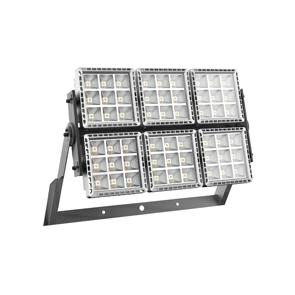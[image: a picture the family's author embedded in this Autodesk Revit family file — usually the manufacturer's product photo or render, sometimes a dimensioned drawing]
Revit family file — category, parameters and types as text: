
# Revit family: Lighting-Floodlights-GEWISS-SMART[PRO]2.0-LED-HIGH-POWER_6MODULE_CLI
name_source: partatom
category: Apparecchi per illuminazione
units: mm (PartAtom-declared; Revit-internal decimal feet)

## family parameters
Condiviso = No
Host = Superficie
Punto di calcolo locali = No
Quota connettore circolare = Usa diametro
Sorgente d'illuminazione = No
Taglio con vuoti quando caricato = No
Tipo di parte = Normale

## types (54) — shared parameters
Application = Indoor / Outdoor
Body = Die-cast aluminium -
Carico apparente = 1020 VA
Catalogue = LIGHTING
Classification: = -
Classificazione = Lighting
Colour = Graphite grey
Colour : = Polyester powder coated
Commenti Wattaggio 1_100 = Sì
Commenti Wattaggio 1_200 = No
Commenti sul wattaggio = 1020W
Context = Sport, Big Areas
Control System = See external supply unit
DIN 18032-3 certification = -
Device with reduced surface temperature = No
Driver = To be ordered separately
Driver Box = External
Eletrical and lighting features = -
Etichetta wattaggio = Sì
External screw = Stainless steel
Fine staffa = 484 mm  [stored 1.58793 ft]
Fixing = Bracket
Gasket = Anti-aging silicone
General information = -
Glow Wire Test : = -
H_centro_STaffa = 459 mm  [stored 1.50591 ft]
IDF = 6be5a8cc-6c55-4606-870e-3d78fd827b65
IDT = 5694ef43a41d4293b3b9519a64b0ddb9
IP degree = IP66
Immagine tipo = SMART PRO 6.jpg
Installationa and maintenance = -
Insulation class = I
LED Maintenance = Yes
L_plafoniera = 817 mm
Lampada = LED
Larghezza = 503 mm  [stored 1.65026 ft]
Lifetime = L90B10 (Tq+25°C) = 36000h L90B10 (Tq+50°C) = 26000h L80B10 (Tq+25°C) = 81000h
Locking Hook = Hexagonal metric screws
Luminaire = LED luminaire with mid and high lumen power
Materials = -
Maximum surface exposed to the wind : = 0,333 m2
Mouting and installation = High-mast lighting - Wall mounting - Ground mouting
N. poli = 2
Operating temperature : = -30 +50 °C
Optic Maintenance = Not available
Optic and illuminating features = -
Ottica_ = GEWISS - OTTICA
Overvoltage protection = See external supply unit
Photobiological Risk Class = -
Produttore = GEWISS S.p.A.
Prospetto di default = 1219 mm
Rated frequency (Hz) = -
SEO = Floodlight
Shield type = Flat tempered glass 4mm
Shock resistance = IK08
Spessore staffa = 59 mm  [stored 0.19357 ft]
Standard- = EN60598-1; EN60598-2-5; IEC 62778; IEC 62471; EN13201
Standards and approvals = -
Stocking temperature = -
Struttura = GEWISS - NERO
Struttura plafoniera = GEWISS - PLAFONIERA
Supply voltage = -
System power = 970W
Technical sheet = https://www.gewiss.com
Tilt- = Rotation on bracket with integrated goniometer
Trasformatore = GEWISS - PLAFONIERA
Type of light source = LED - Not replaceable
URL = https://www.gewiss.com
Unique digital code (Datamatrix) = Currently not present
Version file RFA = 20.11
Vetro acceso = Lampada accesa
Voltaggio = 230 V
Warranty = 5 years
Weight (kg): = 29
Wiring = Watertight connector

## per-type parameters (varying)
| type | Color Rendering Index | Colour temperature | Descrizione | Efficiency (lm/W) | IPEA | Lumen output (lm) | Modello | Optic | Optic : | Standard Deviation Colour Matching | Unified Glare Rating | Versions |
| GWP2630AF757 - SMART PRO 3x2M A2 CRI70 5700K | CRI-70 | 5700K | SMART PRO 3x2M A2 CRI70 5700K | 101 | ROAD = B // LARGE AREAS = A + // CYCLOPEDONALS = A // GREEN AREAS = A // HISTORICAL CENTER = A ++ // OTHER = A ++ | 98200 | GWP2630AF757 | A2 - Asymmetrical Medium | Polished anodised aluminum reflector with 99.99% pure aluminum | SDCM = 5 | G*3 - ULOR = 0 | 5700K cold light |
| GWP2630AH740 - SMART PRO 3x2M C3 CRI70 4000K | CRI-70 | 4000K | SMART PRO 3x2M C3 CRI70 4000K | 126 | ROAD = A + // LARGE AREAS = A4 + // CYCLOPEDONALS = A ++ // GREEN AREAS = A ++ // HISTORICAL CENTER = A5 + // OTHER = A5 + | 122700 | GWP2630AH740 | C3 - Circular 20° | Polished quartz and metallized PC HT reflector | SDCM = 5 | G*6 - ULOR = 0 | 4000K natural light |
| GWP2630AB857 - SMART PRO 3x2M S2 CRI80 5700K | CRI-80 | 5700K | SMART PRO 3x2M S2 CRI80 5700K | 117 | ROAD = A // LARGE AREAS = A3 + // CYCLOPEDONALS = A + // GREEN AREAS = A + // HISTORICAL CENTER = A4 + // OTHER = A4 + | 113700 | GWP2630AB857 | S2 - Symmetric Medium | Polished anodised aluminum reflector with 99.99% pure aluminum | SDCM = 3 | G*6 - ULOR = 0 | 5700K cold light |
| GWP2630AB740 - SMART PRO 3x2M S2 CRI70 4000K | CRI-70 | 4000K | SMART PRO 3x2M S2 CRI70 4000K | 126 | ROAD = A + // LARGE AREAS = A4 + // CYCLOPEDONALS = A ++ // GREEN AREAS = A ++ // HISTORICAL CENTER = A5 + // OTHER = A5 + | 121800 | GWP2630AB740 | S2 - Symmetric Medium | Polished anodised aluminum reflector with 99.99% pure aluminum | SDCM = 5 | G*6 - ULOR = 0 | 4000K natural light |
| GWP2630AC957 - SMART PRO 3x2M A1 CRI90 5700K | CRI-90 TLCI-80 | 5700K | SMART PRO 3x2M A1 CRI90 5700K | 94 | ROAD = C // LARGE AREAS = A // CYCLOPEDONALS = B // GREEN AREAS = B // HISTORICAL CENTER = A + // OTHER = A + | 91400 | GWP2630AC957 | A1 - Asymmetrical Wide | Polished quartz and metallized PC HT reflector | SDCM = 3 | G*4 - ULOR = 0 | 5700K cold light |
| GWP2630AB840 - SMART PRO 3x2M S2 CRI80 4000K | CRI-80 | 4000K | SMART PRO 3x2M S2 CRI80 4000K | 117 | ROAD = A // LARGE AREAS = A3 + // CYCLOPEDONALS = A + // GREEN AREAS = A + // HISTORICAL CENTER = A4 + // OTHER = A4 + | 113700 | GWP2630AB840 | S2 - Symmetric Medium | Polished anodised aluminum reflector with 99.99% pure aluminum | SDCM = 3 | G*6 - ULOR = 0 | 4000K natural light |
| GWP2630AH957 - SMART PRO 3x2M C3 CRI90 5700K | CRI-90 TLCI-80 | 5700K | SMART PRO 3x2M C3 CRI90 5700K | 101 | ROAD = B // LARGE AREAS = A + // CYCLOPEDONALS = A // GREEN AREAS = A // HISTORICAL CENTER = A ++ // OTHER = A ++ | 98200 | GWP2630AH957 | C3 - Circular 20° | Polished quartz and metallized PC HT reflector | SDCM = 3 | G*6 - ULOR = 0 | 5700K cold light |
| GWP2630AL857 - SMART PRO 3x2M C2 CRI80 5700K | CRI-80 | 5700K | SMART PRO 3x2M C2 CRI80 5700K | 115 | ROAD = A // LARGE AREAS = A ++ // CYCLOPEDONALS = A + // GREEN AREAS = A + // HISTORICAL CENTER = A4 + // OTHER = A4 + | 111900 | GWP2630AL857 | C2 - Circular 25° | Polished quartz and metallized PC HT reflector | SDCM = 3 | G*6 - ULOR = 0 | 5700K cold light |
| GWP2630AF857 - SMART PRO 3x2M A2 CRI80 5700K | CRI-80 | 5700K | SMART PRO 3x2M A2 CRI80 5700K | 95 | ROAD = C // LARGE AREAS = A // CYCLOPEDONALS = B // GREEN AREAS = B // HISTORICAL CENTER = A + // OTHER = A + | 91700 | GWP2630AF857 | A2 - Asymmetrical Medium | Polished anodised aluminum reflector with 99.99% pure aluminum | SDCM = 3 | G*3 - ULOR = 0 | 5700K cold light |
| GWP2630AN740 - SMART PRO 3x2M A3 CRI70 4000K | CRI-70 | 4000K | SMART PRO 3x2M A3 CRI70 4000K | 123 | ROAD = A + // LARGE AREAS = A3 + // CYCLOPEDONALS = A ++ // GREEN AREAS = A ++ // HISTORICAL CENTER = A5 + // OTHER = A5 + | 119400 | GWP2630AN740 | A3 - Assymetric Narrow | Polished anodised aluminum reflector with 99.99% pure aluminum | SDCM = 5 | G*6 - ULOR = 0 | 4000K natural light |
| GWP2630AG757 - SMART PRO 3x2M C4 CRI70 5700K | CRI-70 | 5700K | SMART PRO 3x2M C4 CRI70 5700K | 126 | ROAD = A + // LARGE AREAS = A4 + // CYCLOPEDONALS = A ++ // GREEN AREAS = A ++ // HISTORICAL CENTER = A5 + // OTHER = A5 + | 122700 | GWP2630AG757 | C4 - Circular 15° | Polished quartz and metallized PC HT reflector | SDCM = 5 | G*6 - ULOR = 0 | 5700K cold light |
| GWP2630AG840 - SMART PRO 3x2M C4 CRI80 4000K | CRI-80 | 4000K | SMART PRO 3x2M C4 CRI80 4000K | 118 | ROAD = A // LARGE AREAS = A3 + // CYCLOPEDONALS = A + // GREEN AREAS = A + // HISTORICAL CENTER = A4 + // OTHER = A4 + | 114500 | GWP2630AG840 | C4 - Circular 15° | Polished quartz and metallized PC HT reflector | SDCM = 3 | G*6 - ULOR = 0 | 4000K natural light |
| GWP2630AF840 - SMART PRO 3x2M A2 CRI80 4000K | CRI-80 | 4000K | SMART PRO 3x2M A2 CRI80 4000K | 95 | ROAD = C // LARGE AREAS = A // CYCLOPEDONALS = B // GREEN AREAS = B // HISTORICAL CENTER = A + // OTHER = A + | 91700 | GWP2630AF840 | A2 - Asymmetrical Medium | Polished anodised aluminum reflector with 99.99% pure aluminum | SDCM = 3 | G*3 - ULOR = 0 | 4000K natural light |
| GWP2630AM957 - SMART PRO 3x2M C1 CRI90 5700K | CRI-90 TLCI-80 | 5700K | SMART PRO 3x2M C1 CRI90 5700K | 99 | ROAD = C // LARGE AREAS = A // CICLOPEDONALI = B // GREEN AREAS = B // HISTORICAL CENTER = A ++ // OTHER = A ++ | 95900 | GWP2630AM957 | C1 - Circular 30° | Polished quartz and metallized PC HT reflector | SDCM = 3 | G*6 - ULOR = 0 | 5700K cold light |
| GWP2630AN757 - SMART PRO 3x2M A3 CRI70 5700K | CRI-70 | 5700K | SMART PRO 3x2M A3 CRI70 5700K | 123 | ROAD = A + // LARGE AREAS = A3 + // CYCLOPEDONALS = A ++ // GREEN AREAS = A ++ // HISTORICAL CENTER = A5 + // OTHER = A5 + | 119400 | GWP2630AN757 | A3 - Assymetric Narrow | Polished anodised aluminum reflector with 99.99% pure aluminum | SDCM = 5 | G*6 - ULOR = 0 | 5700K cold light |
| GWP2630AM740 - SMART PRO 3x2M C1 CRI70 4000K | CRI-70 | 4000K | SMART PRO 3x2M C1 CRI70 4000K | 124 | ROAD = A + // LARGE AREAS = A3 + // CYCLOPEDONALS = A ++ // GREEN AREAS = A ++ // HISTORICAL CENTER = A5 + // OTHER = A5 + | 119900 | GWP2630AM740 | C1 - Circular 30° | Polished quartz and metallized PC HT reflector | SDCM = 5 | G*6 - ULOR = 0 | 4000K natural light |
| GWP2630AF730 - SMART PRO 3x2M A2 CRI70 3000K | CRI-70 | 3000K | SMART PRO 3x2M A2 CRI70 3000K | 95 | ROAD = C // LARGE AREAS = A // CYCLOPEDONALS = B // GREEN AREAS = B // HISTORICAL CENTER = A + // OTHER = A + | 91700 | GWP2630AF730 | A2 - Asymmetrical Medium | Polished anodised aluminum reflector with 99.99% pure aluminum | SDCM = 5 | G*3 - ULOR = 0 | 3000K warm light |
| GWP2630AL757 - SMART PRO 3x2M C2 CRI70 5700K | CRI-70 | 5700K | SMART PRO 3x2M C2 CRI70 5700K | 124 | ROAD = A + // LARGE AREAS = A3 + // CYCLOPEDONALS = A ++ // GREEN AREAS = A ++ // HISTORICAL CENTER = A5 + // OTHER = A5 + | 119900 | GWP2630AL757 | C2 - Circular 25° | Polished quartz and metallized PC HT reflector | SDCM = 5 | G*6 - ULOR = 0 | 5700K cold light |
| GWP2630AN857 - SMART PRO 3x2M A3 CRI80 5700K | CRI-80 | 5700K | SMART PRO 3x2M A3 CRI80 5700K | 115 | ROAD = A // LARGE AREAS = A ++ // CYCLOPEDONALS = A + // GREEN AREAS = A + // HISTORICAL CENTER = A4 + // OTHER = A4 + | 111400 | GWP2630AN857 | A3 - Assymetric Narrow | Polished anodised aluminum reflector with 99.99% pure aluminum | SDCM = 3 | G*6 - ULOR = 0 | 5700K cold light |
| GWP2630AB957 - SMART PRO 3x2M S2 CRI90 5700K | CRI-90 TLCI-80 | 5700K | SMART PRO 3x2M S2 CRI90 5700K | 100 | ROAD = B // LARGE AREAS = A + // CYCLOPEDONALS = B // GREEN AREAS = B // HISTORICAL CENTER = A ++ // OTHER = A ++ | 97400 | GWP2630AB957 | S2 - Symmetric Medium | Polished anodised aluminum reflector with 99.99% pure aluminum | SDCM = 3 | G*6 - ULOR = 0 | 5700K cold light |
| GWP2630AL730 - SMART PRO 3x2M C2 CRI70 3000K | CRI-70 | 3000K | SMART PRO 3x2M C2 CRI70 3000K | 115 | ROAD = A // LARGE AREAS = A ++ // CYCLOPEDONALS = A + // GREEN AREAS = A + // HISTORICAL CENTER = A4 + // OTHER = A4 + | 111900 | GWP2630AL730 | C2 - Circular 25° | Polished quartz and metallized PC HT reflector | SDCM = 5 | G*6 - ULOR = 0 | 3000K warm light |
| GWP2630AC857 - SMART PRO 3x2M A1 CRI80 5700K | CRI-80 | 5700K | SMART PRO 3x2M A1 CRI80 5700K | 110 | ROAD = A // LARGE AREAS = A ++ // CYCLOPEDONALS = A // GREEN AREAS = A // HISTORICAL CENTER = A3 + // OTHER = A3 + | 106600 | GWP2630AC857 | A1 - Asymmetrical Wide | Polished quartz and metallized PC HT reflector | SDCM = 3 | G*4 - ULOR = 0 | 5700K cold light |
| GWP2630AB730 - SMART PRO 3x2M S2 CRI70 3000K | CRI-70 | 3000K | SMART PRO 3x2M S2 CRI70 3000K | 117 | ROAD = A // LARGE AREAS = A3 + // CYCLOPEDONALS = A + // GREEN AREAS = A + // HISTORICAL CENTER = A4 + // OTHER = A4 + | 113700 | GWP2630AB730 | S2 - Symmetric Medium | Polished anodised aluminum reflector with 99.99% pure aluminum | SDCM = 5 | G*6 - ULOR = 0 | 3000K warm light |
| GWP2630AC730 - SMART PRO 3x2M A1 CRI70 3000K | CRI-70 | 3000K | SMART PRO 3x2M A1 CRI70 3000K | 110 | ROAD = A // LARGE AREAS = A ++ // CYCLOPEDONALS = A // GREEN AREAS = A // HISTORICAL CENTER = A3 + // OTHER = A3 + | 106600 | GWP2630AC730 | A1 - Asymmetrical Wide | Polished quartz and metallized PC HT reflector | SDCM = 5 | G*4 - ULOR = 0 | 3000K warm light |
| GWP2630AA957 - SMART PRO 3x2M S1 CRI90 5700K | CRI-90 TLCI-80 | 5700K | SMART PRO 3x2M S1 CRI90 5700K | 97 | ROAD = C // LARGE AREAS = A // CYCLOPEDONALS = B // GREEN AREAS = B // HISTORICAL CENTER = A + // OTHER = A + | 94100 | GWP2630AA957 | S1 - Symmetric Wide | Polished quartz and metallized PC HT reflector | SDCM = 3 | G*6 - ULOR = 0 | 5700K cold light |
| GWP2630AG957 - SMART PRO 3x2M C4 CRI90 5700K | CRI-90 TLCI-80 | 5700K | SMART PRO 3x2M C4 CRI90 5700K | 101 | ROAD = B // LARGE AREAS = A + // CYCLOPEDONALS = A // GREEN AREAS = A // HISTORICAL CENTER = A ++ // OTHER = A ++ | 98200 | GWP2630AG957 | C4 - Circular 15° | Polished quartz and metallized PC HT reflector | SDCM = 3 | G*6 - ULOR = 0 | 5700K cold light |
| GWP2630AL957 - SMART PRO 3x2M C2 CRI90 5700K | CRI-90 TLCI-80 | 5700K | SMART PRO 3x2M C2 CRI90 5700K | 99 | ROAD = C // LARGE AREAS = A // CICLOPEDONALI = B // GREEN AREAS = B // HISTORICAL CENTER = A ++ // OTHER = A ++ | 95900 | GWP2630AL957 | C2 - Circular 25° | Polished quartz and metallized PC HT reflector | SDCM = 3 | G*6 - ULOR = 0 | 5700K cold light |
| GWP2630AN730 - SMART PRO 3x2M A3 CRI70 3000K | CRI-70 | 3000K | SMART PRO 3x2M A3 CRI70 3000K | 115 | ROAD = A // LARGE AREAS = A ++ // CYCLOPEDONALS = A + // GREEN AREAS = A + // HISTORICAL CENTER = A4 + // OTHER = A4 + | 111400 | GWP2630AN730 | A3 - Assymetric Narrow | Polished anodised aluminum reflector with 99.99% pure aluminum | SDCM = 5 | G*6 - ULOR = 0 | 3000K warm light |
| GWP2630AN957 - SMART PRO 3x2M A3 CRI90 5700K | CRI-90 TLCI-80 | 5700K | SMART PRO 3x2M A3 CRI90 5700K | 98 | ROAD = C // LARGE AREAS = A // CICLOPEDONALI = B // GREEN AREAS = B // HISTORICAL CENTER = A ++ // OTHER = A ++ | 95500 | GWP2630AN957 | A3 - Assymetric Narrow | Polished anodised aluminum reflector with 99.99% pure aluminum | SDCM = 3 | G*6 - ULOR = 0 | 5700K cold light |
| GWP2630AH857 - SMART PRO 3x2M C3 CRI80 5700K | CRI-80 | 5700K | SMART PRO 3x2M C3 CRI80 5700K | 118 | ROAD = A // LARGE AREAS = A3 + // CYCLOPEDONALS = A + // GREEN AREAS = A + // HISTORICAL CENTER = A4 + // OTHER = A4 + | 114500 | GWP2630AH857 | C3 - Circular 20° | Polished quartz and metallized PC HT reflector | SDCM = 3 | G*6 - ULOR = 0 | 5700K cold light |
| GWP2630AF957 - SMART PRO 3x2M A2 CRI90 5700K | CRI-90 TLCI-80 | 5700K | SMART PRO 3x2M A2 CRI90 5700K | 81 | ROAD = D // LARGE AREAS = C // CYCLOPEDONALS = C // GREEN AREAS = C // HISTORICAL CENTER = B // OTHER = B | 78600 | GWP2630AF957 | A2 - Asymmetrical Medium | Polished anodised aluminum reflector with 99.99% pure aluminum | SDCM = 3 | G*3 - ULOR = 0 | 5700K cold light |
| GWP2630AH730 - SMART PRO 3x2M C3 CRI70 3000K | CRI-70 | 3000K | SMART PRO 3x2M C3 CRI70 3000K | 118 | ROAD = A // LARGE AREAS = A3 + // CYCLOPEDONALS = A + // GREEN AREAS = A + // HISTORICAL CENTER = A4 + // OTHER = A4 + | 114500 | GWP2630AH730 | C3 - Circular 20° | Polished quartz and metallized PC HT reflector | SDCM = 5 | G*6 - ULOR = 0 | 3000K warm light |
| GWP2630AL740 - SMART PRO 3x2M C2 CRI70 4000K | CRI-70 | 4000K | SMART PRO 3x2M C2 CRI70 4000K | 124 | ROAD = A + // LARGE AREAS = A3 + // CYCLOPEDONALS = A ++ // GREEN AREAS = A ++ // HISTORICAL CENTER = A5 + // OTHER = A5 + | 119900 | GWP2630AL740 | C2 - Circular 25° | Polished quartz and metallized PC HT reflector | SDCM = 5 | G*6 - ULOR = 0 | 4000K natural light |
| GWP2630AA757 - SMART PRO 3x2M S1 CRI70 5700K | CRI-70 | 5700K | SMART PRO 3x2M S1 CRI70 5700K | 121 | ROAD = A + // LARGE AREAS = A3 + // CYCLOPEDONALS = A ++ // GREEN AREAS = A ++ // HISTORICAL CENTER = A5 + // OTHER = A5 + | 117600 | GWP2630AA757 | S1 - Symmetric Wide | Polished quartz and metallized PC HT reflector | SDCM = 5 | G*6 - ULOR = 0 | 5700K cold light |
| GWP2630AA730 - SMART PRO 3x2M S1 CRI70 3000K | CRI-70 | 3000K | SMART PRO 3x2M S1 CRI70 3000K | 113 | ROAD = A // LARGE AREAS = A ++ // CYCLOPEDONALS = A + // GREEN AREAS = A + // HISTORICAL CENTER = A4 + // OTHER = A4 + | 109800 | GWP2630AA730 | S1 - Symmetric Wide | Polished quartz and metallized PC HT reflector | SDCM = 5 | G*6 - ULOR = 0 | 3000K warm light |
| GWP2630AC740 - SMART PRO 3x2M A1 CRI70 4000K | CRI-70 | 4000K | SMART PRO 3x2M A1 CRI70 4000K | 118 | ROAD = A // LARGE AREAS = A3 + // CYCLOPEDONALS = A + // GREEN AREAS = A + // HISTORICAL CENTER = A4 + // OTHER = A4 + | 114200 | GWP2630AC740 | A1 - Asymmetrical Wide | Polished quartz and metallized PC HT reflector | SDCM = 5 | G*4 - ULOR = 0 | 4000K natural light |
| GWP2630AM857 - SMART PRO 3x2M C1 CRI80 5700K | CRI-80 | 5700K | SMART PRO 3x2M C1 CRI80 5700K | 115 | ROAD = A // LARGE AREAS = A ++ // CYCLOPEDONALS = A + // GREEN AREAS = A + // HISTORICAL CENTER = A4 + // OTHER = A4 + | 111900 | GWP2630AM857 | C1 - Circular 30° | Polished quartz and metallized PC HT reflector | SDCM = 3 | G*6 - ULOR = 0 | 5700K cold light |
| GWP2630AL840 - SMART PRO 3x2M C2 CRI80 4000K | CRI-80 | 4000K | SMART PRO 3x2M C2 CRI80 4000K | 115 | ROAD = A // LARGE AREAS = A ++ // CYCLOPEDONALS = A + // GREEN AREAS = A + // HISTORICAL CENTER = A4 + // OTHER = A4 + | 111900 | GWP2630AL840 | C2 - Circular 25° | Polished quartz and metallized PC HT reflector | SDCM = 3 | G*6 - ULOR = 0 | 4000K natural light |
| GWP2630AN840 - SMART PRO 3x2M A3 CRI80 4000K | CRI-80 | 4000K | SMART PRO 3x2M A3 CRI80 4000K | 115 | ROAD = A // LARGE AREAS = A ++ // CYCLOPEDONALS = A + // GREEN AREAS = A + // HISTORICAL CENTER = A4 + // OTHER = A4 + | 111400 | GWP2630AN840 | A3 - Assymetric Narrow | Polished anodised aluminum reflector with 99.99% pure aluminum | SDCM = 3 | G*6 - ULOR = 0 | 4000K natural light |
| GWP2630AA857 - SMART PRO 3x2M S1 CRI80 5700K | CRI-80 | 5700K | SMART PRO 3x2M S1 CRI80 5700K | 113 | ROAD = A // LARGE AREAS = A ++ // CYCLOPEDONALS = A + // GREEN AREAS = A + // HISTORICAL CENTER = A4 + // OTHER = A4 + | 109800 | GWP2630AA857 | S1 - Symmetric Wide | Polished quartz and metallized PC HT reflector | SDCM = 3 | G*6 - ULOR = 0 | 5700K cold light |
| GWP2630AA840 - SMART PRO 3x2M S1 CRI80 4000K | CRI-80 | 4000K | SMART PRO 3x2M S1 CRI80 4000K | 113 | ROAD = A // LARGE AREAS = A ++ // CYCLOPEDONALS = A + // GREEN AREAS = A + // HISTORICAL CENTER = A4 + // OTHER = A4 + | 109800 | GWP2630AA840 | S1 - Symmetric Wide | Polished quartz and metallized PC HT reflector | SDCM = 3 | G*6 - ULOR = 0 | 4000K natural light |
| GWP2630AB757 - SMART PRO 3x2M S2 CRI70 5700K | CRI-70 | 5700K | SMART PRO 3x2M S2 CRI70 5700K | 126 | ROAD = A + // LARGE AREAS = A4 + // CYCLOPEDONALS = A ++ // GREEN AREAS = A ++ // HISTORICAL CENTER = A5 + // OTHER = A5 + | 121800 | GWP2630AB757 | S2 - Symmetric Medium | Polished anodised aluminum reflector with 99.99% pure aluminum | SDCM = 5 | G*6 - ULOR = 0 | 5700K cold light |
| GWP2630AM840 - SMART PRO 3x2M C1 CRI80 4000K | CRI-80 | 4000K | SMART PRO 3x2M C1 CRI80 4000K | 115 | ROAD = A // LARGE AREAS = A ++ // CYCLOPEDONALS = A + // GREEN AREAS = A + // HISTORICAL CENTER = A4 + // OTHER = A4 + | 111900 | GWP2630AM840 | C1 - Circular 30° | Polished quartz and metallized PC HT reflector | SDCM = 3 | G*6 - ULOR = 0 | 4000K natural light |
| GWP2630AG857 - SMART PRO 3x2M C4 CRI80 5700K | CRI-80 | 5700K | SMART PRO 3x2M C4 CRI80 5700K | 118 | ROAD = A // LARGE AREAS = A3 + // CYCLOPEDONALS = A + // GREEN AREAS = A + // HISTORICAL CENTER = A4 + // OTHER = A4 + | 114500 | GWP2630AG857 | C4 - Circular 15° | Polished quartz and metallized PC HT reflector | SDCM = 3 | G*6 - ULOR = 0 | 5700K cold light |
| GWP2630AC840 - SMART PRO 3x2M A1 CRI80 4000K | CRI-80 | 4000K | SMART PRO 3x2M A1 CRI80 4000K | 110 | ROAD = A // LARGE AREAS = A ++ // CYCLOPEDONALS = A // GREEN AREAS = A // HISTORICAL CENTER = A3 + // OTHER = A3 + | 106600 | GWP2630AC840 | A1 - Asymmetrical Wide | Polished quartz and metallized PC HT reflector | SDCM = 3 | G*4 - ULOR = 0 | 4000K natural light |
| GWP2630AG740 - SMART PRO 3x2M C4 CRI70 4000K | CRI-70 | 4000K | SMART PRO 3x2M C4 CRI70 4000K | 126 | ROAD = A + // LARGE AREAS = A4 + // CYCLOPEDONALS = A ++ // GREEN AREAS = A ++ // HISTORICAL CENTER = A5 + // OTHER = A5 + | 122700 | GWP2630AG740 | C4 - Circular 15° | Polished quartz and metallized PC HT reflector | SDCM = 5 | G*6 - ULOR = 0 | 4000K natural light |
| GWP2630AC757 - SMART PRO 3x2M A1 CRI70 5700K | CRI-70 | 5700K | SMART PRO 3x2M A1 CRI70 5700K | 118 | ROAD = A // LARGE AREAS = A3 + // CYCLOPEDONALS = A + // GREEN AREAS = A + // HISTORICAL CENTER = A4 + // OTHER = A4 + | 114200 | GWP2630AC757 | A1 - Asymmetrical Wide | Polished quartz and metallized PC HT reflector | SDCM = 5 | G*4 - ULOR = 0 | 5700K cold light |
| GWP2630AM730 - SMART PRO 3x2M C1 CRI70 3000K | CRI-70 | 3000K | SMART PRO 3x2M C1 CRI70 3000K | 115 | ROAD = A // LARGE AREAS = A ++ // CYCLOPEDONALS = A + // GREEN AREAS = A + // HISTORICAL CENTER = A4 + // OTHER = A4 + | 111900 | GWP2630AM730 | C1 - Circular 30° | Polished quartz and metallized PC HT reflector | SDCM = 5 | G*6 - ULOR = 0 | 3000K warm light |
| GWP2630AH757 - SMART PRO 3x2M C3 CRI70 5700K | CRI-70 | 5700K | SMART PRO 3x2M C3 CRI70 5700K | 126 | ROAD = A + // LARGE AREAS = A4 + // CYCLOPEDONALS = A ++ // GREEN AREAS = A ++ // HISTORICAL CENTER = A5 + // OTHER = A5 + | 122700 | GWP2630AH757 | C3 - Circular 20° | Polished quartz and metallized PC HT reflector | SDCM = 5 | G*6 - ULOR = 0 | 5700K cold light |
| GWP2630AG730 - SMART PRO 3x2M C4 CRI70 3000K | CRI-70 | 3000K | SMART PRO 3x2M C4 CRI70 3000K | 118 | ROAD = A // LARGE AREAS = A3 + // CYCLOPEDONALS = A + // GREEN AREAS = A + // HISTORICAL CENTER = A4 + // OTHER = A4 + | 114500 | GWP2630AG730 | C4 - Circular 15° | Polished quartz and metallized PC HT reflector | SDCM = 5 | G*6 - ULOR = 0 | 3000K warm light |
| GWP2630AH840 - SMART PRO 3x2M C3 CRI80 4000K | CRI-80 | 4000K | SMART PRO 3x2M C3 CRI80 4000K | 118 | ROAD = A // LARGE AREAS = A3 + // CYCLOPEDONALS = A + // GREEN AREAS = A + // HISTORICAL CENTER = A4 + // OTHER = A4 + | 114500 | GWP2630AH840 | C3 - Circular 20° | Polished quartz and metallized PC HT reflector | SDCM = 3 | G*6 - ULOR = 0 | 4000K natural light |
| GWP2630AM757 - SMART PRO 3x2M C1 CRI70 5700K | CRI-70 | 5700K | SMART PRO 3x2M C1 CRI70 5700K | 124 | ROAD = A + // LARGE AREAS = A3 + // CYCLOPEDONALS = A ++ // GREEN AREAS = A ++ // HISTORICAL CENTER = A5 + // OTHER = A5 + | 119900 | GWP2630AM757 | C1 - Circular 30° | Polished quartz and metallized PC HT reflector | SDCM = 5 | G*6 - ULOR = 0 | 5700K cold light |
| GWP2630AA740 - SMART PRO 3x2M S1 CRI70 4000K | CRI-70 | 4000K | SMART PRO 3x2M S1 CRI70 4000K | 121 | ROAD = A + // LARGE AREAS = A3 + // CYCLOPEDONALS = A ++ // GREEN AREAS = A ++ // HISTORICAL CENTER = A5 + // OTHER = A5 + | 117600 | GWP2630AA740 | S1 - Symmetric Wide | Polished quartz and metallized PC HT reflector | SDCM = 5 | G*6 - ULOR = 0 | 4000K natural light |
| GWP2630AF740 - SMART PRO 3x2M A2 CRI70 4000K | CRI-70 | 4000K | SMART PRO 3x2M A2 CRI70 4000K | 101 | ROAD = B // LARGE AREAS = A + // CYCLOPEDONALS = A // GREEN AREAS = A // HISTORICAL CENTER = A ++ // OTHER = A ++ | 98200 | GWP2630AF740 | A2 - Asymmetrical Medium | Polished anodised aluminum reflector with 99.99% pure aluminum | SDCM = 5 | G*3 - ULOR = 0 | 4000K natural light |

note: [stored X ft] marks values corroborated as IEEE doubles in the binary element streams (Revit-internal decimal feet)

## geometry (parser evidence)
native form markers: Blend x2
no freeform markers — native parametric forms only
